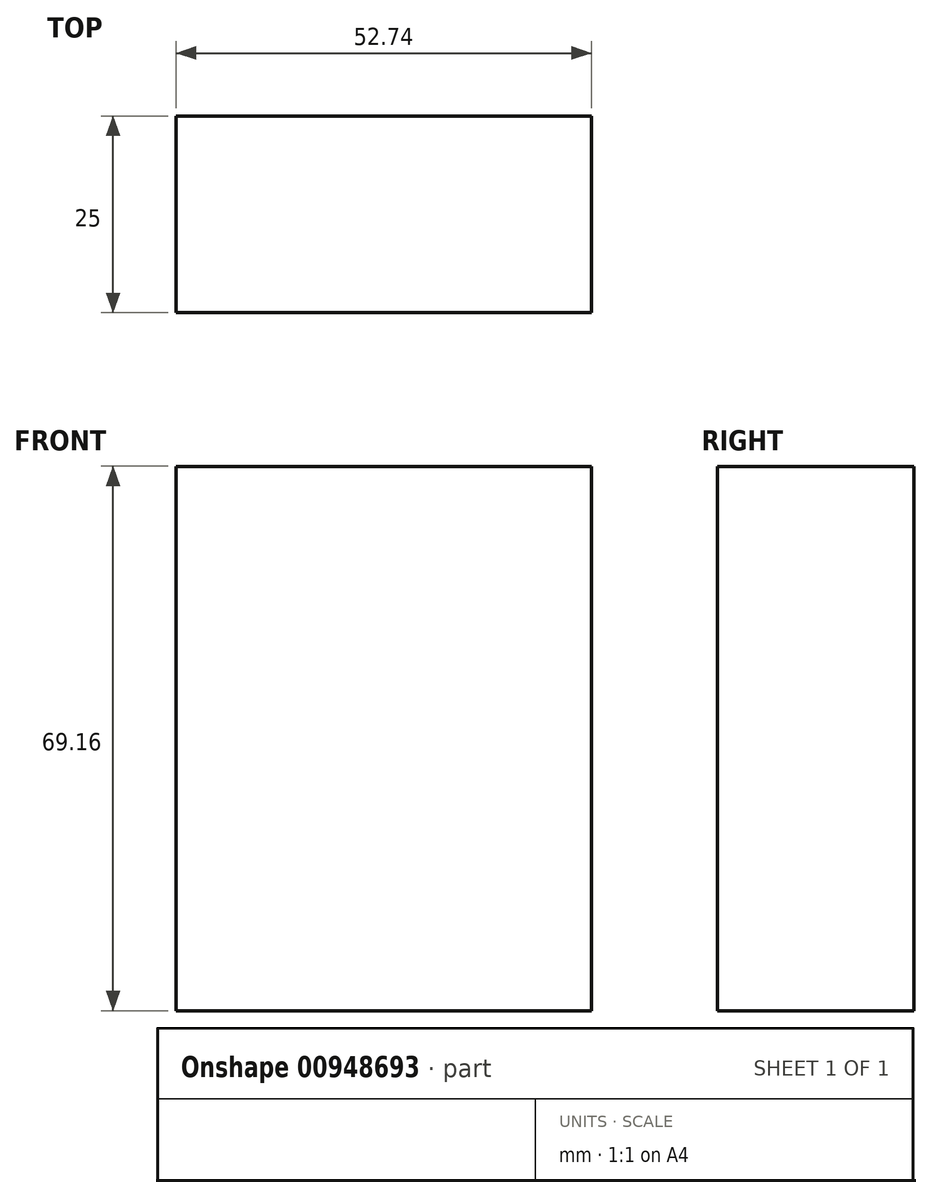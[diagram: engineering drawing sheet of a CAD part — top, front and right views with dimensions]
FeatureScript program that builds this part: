
annotation { "Feature Type Name" : "Feature", "Feature Type Description" : "" }
export const myFeature = defineFeature(function(context is Context, id is Id, definition is map)
    precondition{}
    {
        {
            var Q0;
            Q0=qCreatedBy(makeId("Front.planeOp"),FACE);
            var sketch = newSketch(context, id + "F0", { "sketchPlane" : qUnion([Q0])});
            skLineSegment(sketch, "E0.bottom", {"start": v(-27.15, 40.4) * mm, "end": v(25.59, 40.4) * mm});
            skLineSegment(sketch, "E0.top", {"start": v(-27.15, -28.75) * mm, "end": v(25.59, -28.75) * mm});
            skLineSegment(sketch, "E0.left", {"start": v(-27.15, 40.4) * mm, "end": v(-27.15, -28.75) * mm});
            skLineSegment(sketch, "E0.right", {"start": v(25.59, 40.4) * mm, "end": v(25.59, -28.75) * mm});
            skSolve(sketch);
        }
        {
            var Q0;
            Q0 = qSketchRegion(id + "F0", true);
            extrude(context, id + "F1", {"entities" : qUnion([Q0]), "depth" : 25 * mm, "offsetDistance" : 25 * mm});
        }
    });
